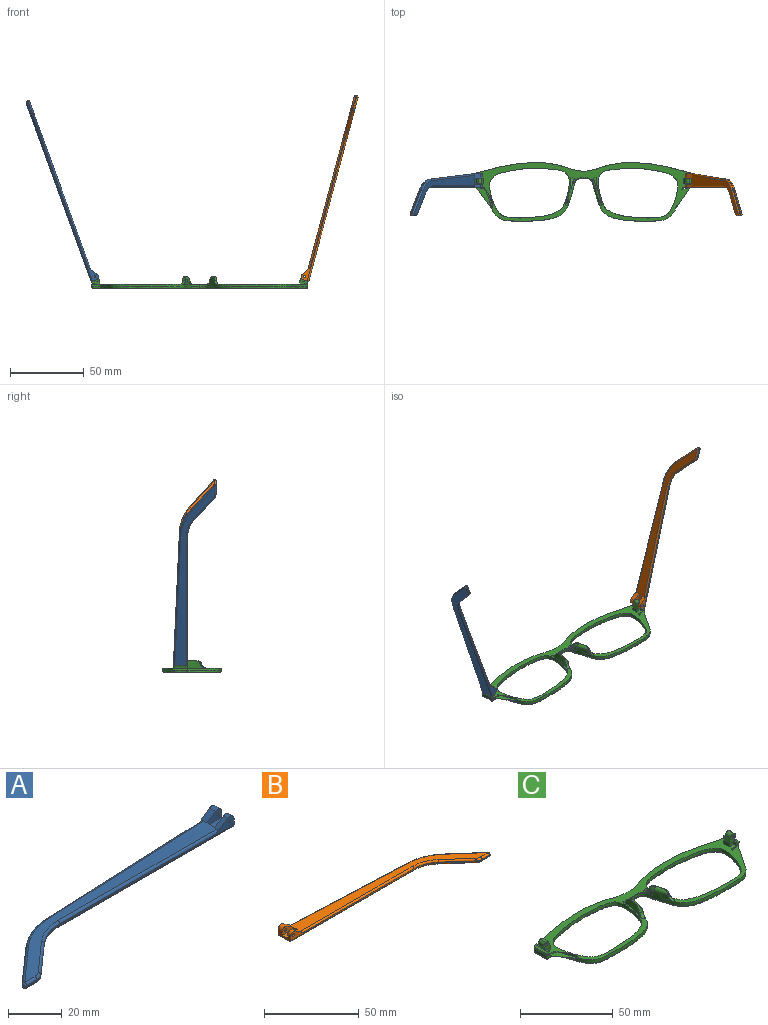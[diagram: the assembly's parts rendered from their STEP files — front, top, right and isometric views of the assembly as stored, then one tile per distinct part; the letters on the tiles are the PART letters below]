
ASSEMBLY  parts=3 mates=2
PART A: 43 faces, bbox 130.2x29.5x5.9 mm
  f0: plane 9.62x3.72mm, normal (1,0,0), area 24.7mm2, adj f1,f3,f4,f5,f10,f16,f18,f28
  f1: cylinder r=2.2mm len=3.45mm, axis (0,-1,0), area 11mm2, adj f0,f2,f4,f37
  f2: plane 6.01x3.91mm, normal (-0.55,0,0.84), area 12.7mm2, adj f1,f4,f9,f19,f37
  f3: plane 2.26x0.1mm, normal (0,0,1), area 0.1mm2, adj f0,f5,f18
  f4: plane 92.1x4.9mm, normal (0,-1,0), area 79.9mm2, adj f0,f1,f2,f14,f19,f36,f42
  f5: plane 93.42x4.13mm, normal (-0.04,1,0), area 64.8mm2, adj f0,f3,f11,f15,f17,f27,f28
  f6: plane 17.82x15.72mm, normal (-0.66,0.75,0), area 14.3mm2, adj f11,f12,f25,f30
  f7: plane 5.46x0.6mm, normal (0,-1,0), area 3.3mm2, adj f12,f13,f23,f32
  f8: plane 14.99x13.23mm, normal (0.66,-0.75,0), area 12mm2, adj f13,f14,f21,f34
  f9: plane 121.18x26.73mm, normal (0,0,1), area 627.7mm2, adj f2,f17,f19,f20,f21,f22,f23,f25
  f10: plane 129.1x27.08mm, normal (0,0,-1), area 686.5mm2, adj f0,f28,f29,f30,f32,f33,f34,f35
  f11: cylinder r=30mm len=18.52mm, axis (0,0,-1), area 12.2mm2, adj f5,f6,f26,f29
  f12: cylinder r=1mm len=1.75mm, axis (0,0,-1), area 1.5mm2, adj f6,f7,f24,f31
  f13: cylinder r=5mm len=3.31mm, axis (0,0,-1), area 2.2mm2, adj f7,f8,f22,f33
  f14: cylinder r=20mm len=13.23mm, axis (0,0,1), area 8.7mm2, adj f4,f8,f20,f35
  f15: plane 5.66x0.25mm, normal (0,0,-1), area 0.7mm2, adj f5,f17,f18
  f16: cylinder r=2.2mm len=3.45mm, axis (0,-1,0), area 14.8mm2, adj f0,f17,f18,f38
  f17: plane 6.01x3.91mm, normal (-0.55,0,0.84), area 16.9mm2, adj f5,f9,f15,f16,f18,f27,f38
  f18: plane 7.92x3.3mm, normal (0,1,0), area 15.9mm2, adj f0,f3,f15,f16,f17,f41
  f19: cylinder r=1mm len=84.18mm, axis (-1,0,0), area 131.4mm2, adj f2,f4,f9,f20
  f20: torus R=21mm, axis (0,0,1), area 23.1mm2, adj f9,f14,f19,f21
  f21: cylinder r=1mm len=15.65mm, axis (-0.75,-0.66,0), area 31.4mm2, adj f8,f9,f20,f22
  f22: torus R=4mm, axis (0,0,1), area 5.3mm2, adj f9,f13,f21,f23
  f23: cylinder r=1mm len=5.46mm, axis (-1,0,0), area 8.6mm2, adj f7,f9,f22,f24
  f24: sphere r=1mm, area 2.4mm2, adj f12,f23,f25
  f25: cylinder r=1mm len=18.48mm, axis (0.75,0.66,0), area 37.3mm2, adj f6,f9,f24,f26
  f26: torus R=29mm, axis (0,0,1), area 31.6mm2, adj f9,f11,f25,f27
  f27: cylinder r=1mm len=85.5mm, axis (1,0.04,0), area 133.5mm2, adj f5,f9,f17,f26
  f28: cylinder r=1mm len=93.46mm, axis (-1,-0.04,0), area 146.9mm2, adj f0,f5,f10,f29
  f29: torus R=29mm, axis (0,0,1), area 31.6mm2, adj f10,f11,f28,f30
  f30: cylinder r=1mm len=18.48mm, axis (-0.75,-0.66,0), area 37.3mm2, adj f6,f10,f29,f31
  f31: sphere r=1mm, area 2.4mm2, adj f12,f30,f32
  f32: cylinder r=1mm len=5.46mm, axis (1,0,0), area 8.6mm2, adj f7,f10,f31,f33
  f33: torus R=4mm, axis (0,0,1), area 5.3mm2, adj f10,f13,f32,f34
  f34: cylinder r=1mm len=15.65mm, axis (0.75,0.66,0), area 31.4mm2, adj f8,f10,f33,f35
  f35: torus R=21mm, axis (0,0,1), area 23.1mm2, adj f10,f14,f34,f36
  f36: cylinder r=1mm len=92.1mm, axis (1,0,0), area 144.7mm2, adj f0,f4,f10,f35
  f37: plane 7.92x4.7mm, normal (0,1,0), area 27mm2, adj f0,f1,f2,f39,f40,f42
  f38: plane 7.92x4.7mm, normal (0,-1,0), area 27mm2, adj f0,f16,f17,f39,f40,f41
  f39: plane 7.92x4.1mm, normal (0,0,1), area 32.5mm2, adj f0,f37,f38,f40
  f40: plane 4.1x1.4mm, normal (1,0,0), area 5.7mm2, adj f9,f37,f38,f39
  f41: cylinder r=0.5mm len=3.1mm, axis (0,-1,0), area 9.7mm2, adj f18,f38
  f42: cylinder r=0.5mm len=2.3mm, axis (0,-1,0), area 7.2mm2, adj f4,f37
PART B: 43 faces, bbox 130.2x29.5x5.9 mm
  f0: plane 9.62x3.72mm, normal (-1,0,0), area 24.7mm2, adj f1,f3,f4,f5,f10,f16,f18,f28
  f1: cylinder r=2.2mm len=3.45mm, axis (0,-1,0), area 11mm2, adj f0,f2,f4,f37
  f2: plane 6.01x3.91mm, normal (0.55,0,0.84), area 12.7mm2, adj f1,f4,f9,f19,f37
  f3: plane 2.26x0.1mm, normal (0,0,1), area 0.1mm2, adj f0,f5,f18
  f4: plane 92.1x4.9mm, normal (0,-1,0), area 78.2mm2, adj f0,f1,f2,f14,f19,f36,f42
  f5: plane 93.42x4.13mm, normal (0.04,1,0), area 64.8mm2, adj f0,f3,f11,f15,f17,f27,f28
  f6: plane 17.82x15.72mm, normal (0.66,0.75,0), area 14.3mm2, adj f11,f12,f25,f30
  f7: plane 5.46x0.6mm, normal (0,-1,0), area 3.3mm2, adj f12,f13,f23,f32
  f8: plane 14.99x13.23mm, normal (-0.66,-0.75,0), area 12mm2, adj f13,f14,f21,f34
  f9: plane 121.18x26.73mm, normal (0,0,1), area 627.7mm2, adj f2,f17,f19,f20,f21,f22,f23,f25
  f10: plane 129.1x27.08mm, normal (0,0,-1), area 686.5mm2, adj f0,f28,f29,f30,f32,f33,f34,f35
  f11: cylinder r=30mm len=18.52mm, axis (0,0,-1), area 12.2mm2, adj f5,f6,f26,f29
  f12: cylinder r=1mm len=1.75mm, axis (0,0,-1), area 1.5mm2, adj f6,f7,f24,f31
  f13: cylinder r=5mm len=3.31mm, axis (0,0,-1), area 2.2mm2, adj f7,f8,f22,f33
  f14: cylinder r=20mm len=13.23mm, axis (0,0,1), area 8.7mm2, adj f4,f8,f20,f35
  f15: plane 5.66x0.25mm, normal (0,0,-1), area 0.7mm2, adj f5,f17,f18
  f16: cylinder r=2.2mm len=3.45mm, axis (0,-1,0), area 14.8mm2, adj f0,f17,f18,f38
  f17: plane 6.01x3.91mm, normal (0.55,0,0.84), area 16.9mm2, adj f5,f9,f15,f16,f18,f27,f38
  f18: plane 7.92x3.3mm, normal (0,1,0), area 14.3mm2, adj f0,f3,f15,f16,f17,f41
  f19: cylinder r=1mm len=84.18mm, axis (1,0,0), area 131.4mm2, adj f2,f4,f9,f20
  f20: torus R=21mm, axis (0,0,1), area 23.1mm2, adj f9,f14,f19,f21
  f21: cylinder r=1mm len=15.65mm, axis (0.75,-0.66,0), area 31.4mm2, adj f8,f9,f20,f22
  f22: torus R=4mm, axis (0,0,1), area 5.3mm2, adj f9,f13,f21,f23
  f23: cylinder r=1mm len=5.46mm, axis (1,0,0), area 8.6mm2, adj f7,f9,f22,f24
  f24: sphere r=1mm, area 2.4mm2, adj f12,f23,f25
  f25: cylinder r=1mm len=18.48mm, axis (-0.75,0.66,0), area 37.3mm2, adj f6,f9,f24,f26
  f26: torus R=29mm, axis (0,0,1), area 31.6mm2, adj f9,f11,f25,f27
  f27: cylinder r=1mm len=85.5mm, axis (-1,0.04,0), area 133.5mm2, adj f5,f9,f17,f26
  f28: cylinder r=1mm len=93.46mm, axis (1,-0.04,0), area 146.9mm2, adj f0,f5,f10,f29
  f29: torus R=29mm, axis (0,0,1), area 31.6mm2, adj f10,f11,f28,f30
  f30: cylinder r=1mm len=18.48mm, axis (0.75,-0.66,0), area 37.3mm2, adj f6,f10,f29,f31
  f31: sphere r=1mm, area 2.4mm2, adj f12,f30,f32
  f32: cylinder r=1mm len=5.46mm, axis (-1,0,0), area 8.6mm2, adj f7,f10,f31,f33
  f33: torus R=4mm, axis (0,0,1), area 5.3mm2, adj f10,f13,f32,f34
  f34: cylinder r=1mm len=15.65mm, axis (-0.75,0.66,0), area 31.4mm2, adj f8,f10,f33,f35
  f35: torus R=21mm, axis (0,0,1), area 23.1mm2, adj f10,f14,f34,f36
  f36: cylinder r=1mm len=92.1mm, axis (-1,0,0), area 144.7mm2, adj f0,f4,f10,f35
  f37: plane 7.92x4.7mm, normal (0,1,0), area 25.4mm2, adj f0,f1,f2,f39,f40,f42
  f38: plane 7.92x4.7mm, normal (0,-1,0), area 25.4mm2, adj f0,f16,f17,f39,f40,f41
  f39: plane 7.92x4.1mm, normal (0,0,1), area 32.5mm2, adj f0,f37,f38,f40
  f40: plane 4.1x1.4mm, normal (-1,0,0), area 5.7mm2, adj f9,f37,f38,f39
  f41: cylinder r=0.88mm len=3.1mm, axis (0,-1,0), area 17mm2, adj f18,f38
  f42: cylinder r=0.88mm len=2.3mm, axis (0,-1,0), area 12.6mm2, adj f4,f37
PART C: 98 faces, bbox 148.1x40.9x10.4 mm
  f0: bspline ~1.82x1.22mm, area 0.7mm2, adj f2,f6,f35,f42
  f1: plane 147.39x40.16mm, normal (0,0,1), area 1084.3mm2, adj f3,f4,f5,f6,f7,f8,f18,f21
  f2: bspline ~6.08x4.93mm, area 12.6mm2, adj f0,f6,f35,f39,f41,f42,f43
  f3: plane 1.23x0.04mm, normal (0,0,1), area 0mm2, adj f1,f6,f20
  f4: plane 6.97x5.07mm, normal (0,1,0), area 22.7mm2, adj f1,f18,f19,f23,f25,f26,f28,f29
  f5: plane 3.2x2.36mm, normal (0,-1,0), area 5.7mm2, adj f1,f18,f24,f27
  f6: extruded ~73.26x39.84mm, area 292.7mm2, adj f0,f1,f2,f3,f7,f10,f11,f12
  f7: extruded ~35.39x5.69mm, area 72.2mm2, adj f1,f6,f16,f56
  f8: extruded ~54.09x33.88mm, area 294.3mm2, adj f1,f17
  f9: plane 144.78x37.85mm, normal (0,0,-1), area 582.4mm2, adj f11,f13,f15,f16,f17,f59,f61,f63
  f10: plane 4.46x1.45mm, normal (0,0,1), area 0.1mm2, adj f6,f36
  f11: bspline ~73.27x30.39mm, area 161.7mm2, adj f6,f9,f12,f59
  f12: bspline ~1x1mm, area 0.8mm2, adj f6,f11,f13
  f13: bspline ~8.99x1.23mm, area 12.6mm2, adj f6,f9,f12,f14
  f14: bspline ~1.04x1mm, area 0.7mm2, adj f6,f13,f15
  f15: bspline ~45.86x8.59mm, area 59.8mm2, adj f6,f9,f14,f16
  f16: bspline ~37.01x6.7mm, area 56.6mm2, adj f7,f9,f15,f64
  f17: bspline ~56.23x35.9mm, area 235.3mm2, adj f8,f9
  f18: plane 4x2.36mm, normal (-1,0,0), area 9.5mm2, adj f1,f4,f5,f19
  f19: plane 4x0.02mm, normal (0.34,0,0.94), area 0.1mm2, adj f4,f18,f26
  f20: plane 2.76x2.53mm, normal (0,-1,0), area 3.9mm2, adj f3,f24,f25,f33,f46
  f21: plane 7.67x1.6mm, normal (0.94,0,-0.34), area 13mm2, adj f1,f33,f34,f46
  f22: plane 2.1x1.69mm, normal (0,1,0), area 2.8mm2, adj f1,f23,f25,f34,f46
  f23: plane 3.3x2.1mm, normal (-1,0,0), area 6.9mm2, adj f1,f4,f22,f25
  f24: plane 2.35x2.1mm, normal (-1,0,0), area 4.9mm2, adj f1,f5,f20,f25,f27
  f25: plane 9.65x1.24mm, normal (0,0,1), area 8.2mm2, adj f4,f20,f22,f23,f24,f27,f28,f46
  f26: plane 4x3.31mm, normal (-0.94,0,0.34), area 14.1mm2, adj f4,f19,f27,f30
  f27: plane 5.77x5.06mm, normal (0,-1,0), area 17mm2, adj f5,f24,f25,f26,f28,f29,f30,f31
  f28: plane 4x2.21mm, normal (0.94,0,-0.34), area 9.4mm2, adj f4,f25,f27,f31
  f29: plane 4x0.01mm, normal (0.34,0,0.94), area 0mm2, adj f4,f27,f30,f31
  f30: cylinder r=1.98mm len=4mm, axis (0,1,0), area 12.4mm2, adj f4,f26,f27,f29
  f31: cylinder r=1.98mm len=4mm, axis (0,-1,0), area 12.4mm2, adj f4,f27,f28,f29
  f32: cylinder r=0.88mm len=4mm, axis (0,-1,0), area 22mm2, adj f4,f27
  f33: cone r=1mm half-angle=20deg, axis (0,0,1), area 2.3mm2, adj f1,f20,f21,f46
  f34: cylinder r=1mm len=2.28mm, axis (-0.34,0,-0.94), area 3mm2, adj f1,f21,f22,f46
  f35: extruded ~3.67x3.12mm, area 6mm2, adj f0,f2,f6,f49
  f36: extruded ~4.44x3.32mm, area 15.1mm2, adj f6,f10,f40,f41,f45
  f37: extruded ~18.78x5mm, area 59.7mm2, adj f1,f38,f39,f40,f44,f45
  f38: plane 4.99x1.44mm, normal (0,0,1), area 0.6mm2, adj f37,f39,f40,f41
  f39: bspline ~8.14x4.17mm, area 6.4mm2, adj f2,f37,f38,f44
  f40: bspline ~6.59x5.19mm, area 6.8mm2, adj f36,f37,f38,f41,f45
  f41: bspline ~9.7x4.68mm, area 21.5mm2, adj f2,f6,f36,f38,f40
  f42: bspline ~2.67x2.04mm, area 1.9mm2, adj f0,f2,f6,f43,f48
  f43: bspline ~3.55x3.47mm, area 3.7mm2, adj f1,f2,f42,f44,f48
  f44: bspline ~5.69x4.37mm, area 6.9mm2, adj f1,f37,f39,f43
  f45: bspline ~4.01x3.8mm, area 7.6mm2, adj f1,f6,f36,f37,f40
  f46: plane 9.71x1.44mm, normal (0.34,0,0.94), area 13.9mm2, adj f20,f21,f22,f25,f33,f34
  f47: bspline ~6.38x2.14mm, area 2.6mm2, adj f1,f6,f48,f95
  f48: bspline ~2.1x1.46mm, area 0.6mm2, adj f6,f42,f43,f47
  f49: bspline ~5.24x1.75mm, area 0mm2, adj f6,f35
  f50: bspline ~2.19x1.4mm, area 0.7mm2, adj f51,f55,f83,f90
  f51: bspline ~6.08x4.93mm, area 12.6mm2, adj f50,f55,f83,f87,f89,f90,f91
  f52: plane 1.23x0.04mm, normal (0,0,1), area 0mm2, adj f1,f55,f68
  f53: plane 6.97x5.07mm, normal (0,1,0), area 22.7mm2, adj f1,f66,f67,f71,f73,f74,f76,f77
  f54: plane 3.2x2.36mm, normal (0,-1,0), area 5.7mm2, adj f1,f66,f72,f75
  f55: extruded ~73.26x39.84mm, area 292.7mm2, adj f1,f6,f50,f51,f52,f56,f58,f59
  f56: extruded ~35.39x5.69mm, area 72.2mm2, adj f1,f7,f55,f64
  f57: extruded ~54.09x33.88mm, area 294.3mm2, adj f1,f65
  f58: plane 4.46x1.45mm, normal (0,0,1), area 0.1mm2, adj f55,f84
  f59: bspline ~73.83x30.39mm, area 161.7mm2, adj f9,f11,f55,f60
  f60: bspline ~1x1mm, area 0.8mm2, adj f55,f59,f61
  f61: bspline ~8.99x1.23mm, area 12.6mm2, adj f9,f55,f60,f62
  f62: bspline ~1.04x1mm, area 0.8mm2, adj f55,f61,f63
  f63: bspline ~45.86x8.59mm, area 59.8mm2, adj f9,f55,f62,f64
  f64: bspline ~37.01x6.7mm, area 56.6mm2, adj f9,f16,f56,f63
  f65: bspline ~56.22x35.9mm, area 235.3mm2, adj f9,f57
  f66: plane 4x2.36mm, normal (1,0,0), area 9.5mm2, adj f1,f53,f54,f67
  f67: plane 4x0.02mm, normal (-0.34,0,0.94), area 0.1mm2, adj f53,f66,f74
  f68: plane 2.76x2.53mm, normal (0,-1,0), area 3.9mm2, adj f52,f72,f73,f81,f94
  f69: plane 7.67x1.6mm, normal (-0.94,0,-0.34), area 13mm2, adj f1,f81,f82,f94
  f70: plane 2.1x1.69mm, normal (0,1,0), area 2.8mm2, adj f1,f71,f73,f82,f94
  f71: plane 3.3x2.1mm, normal (1,0,0), area 6.9mm2, adj f1,f53,f70,f73
  f72: plane 2.35x2.1mm, normal (1,0,0), area 4.9mm2, adj f1,f54,f68,f73,f75
  f73: plane 9.65x1.24mm, normal (0,0,1), area 8.2mm2, adj f53,f68,f70,f71,f72,f75,f76,f94
  f74: plane 4x3.31mm, normal (0.94,0,0.34), area 14.1mm2, adj f53,f67,f75,f78
  f75: plane 5.77x5.06mm, normal (0,-1,0), area 17mm2, adj f54,f72,f73,f74,f76,f77,f78,f79
  f76: plane 4x2.21mm, normal (-0.94,0,-0.34), area 9.4mm2, adj f53,f73,f75,f79
  f77: plane 4x0.01mm, normal (-0.34,0,0.94), area 0mm2, adj f53,f75,f78,f79
  f78: cylinder r=1.98mm len=4mm, axis (0,1,0), area 12.4mm2, adj f53,f74,f75,f77
  f79: cylinder r=1.98mm len=4mm, axis (0,-1,0), area 12.4mm2, adj f53,f75,f76,f77
  f80: cylinder r=0.88mm len=4mm, axis (0,-1,0), area 22mm2, adj f53,f75
  f81: cone r=1mm half-angle=20deg, axis (0,0,1), area 2.3mm2, adj f1,f68,f69,f94
  f82: cylinder r=1mm len=2.28mm, axis (0.34,0,-0.94), area 3mm2, adj f1,f69,f70,f94
  f83: extruded ~3.67x3.12mm, area 6mm2, adj f50,f51,f55,f97
  f84: extruded ~4.44x3.32mm, area 15.1mm2, adj f55,f58,f88,f89,f93
  f85: extruded ~18.78x5mm, area 59.7mm2, adj f1,f86,f87,f88,f92,f93
  f86: plane 4.99x1.44mm, normal (0,0,1), area 0.6mm2, adj f85,f87,f88,f89
  f87: bspline ~8.14x4.17mm, area 6.4mm2, adj f51,f85,f86,f92
  f88: bspline ~6.59x5.19mm, area 6.8mm2, adj f84,f85,f86,f89,f93
  f89: bspline ~10.82x4.98mm, area 21.5mm2, adj f51,f55,f84,f86,f88
  f90: bspline ~2.66x2.04mm, area 1.9mm2, adj f50,f51,f55,f91,f96
  f91: bspline ~3.55x3.47mm, area 3.7mm2, adj f1,f51,f90,f92,f96
  f92: bspline ~5.15x4.19mm, area 6.9mm2, adj f1,f85,f87,f91
  f93: bspline ~4.01x3.8mm, area 7.6mm2, adj f1,f55,f84,f85,f88
  f94: plane 9.71x1.44mm, normal (-0.34,0,0.94), area 13.9mm2, adj f68,f69,f70,f73,f81,f82
  f95: bspline ~6.38x2.14mm, area 2.6mm2, adj f1,f47,f55,f96
  f96: bspline ~2.1x1.46mm, area 0.6mm2, adj f55,f90,f91,f95
  f97: bspline ~5.24x1.75mm, area 0mm2, adj f55,f83
PLACE A rot(axis=(0,1,0),70deg) t=(-84.77,-5.75,56)mm
PLACE B rot(axis=(0,-1,0),75deg) t=(68.2,-5.75,-61.61)mm
PLACE C t=(10.15,-1.13,-5.77)mm
MATE revolute A.f1 <-> C.f78  axis (0,-1,0) through (-60.89,2.72,1.22)mm
MATE revolute B.f41 <-> C.f31  axis (0,-1,0) through (81.2,2.72,1.21)mm
